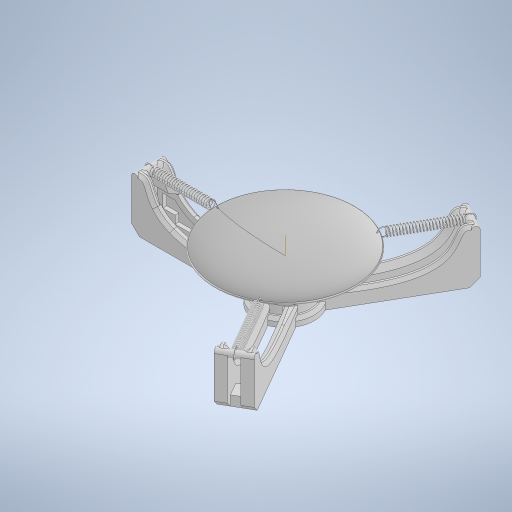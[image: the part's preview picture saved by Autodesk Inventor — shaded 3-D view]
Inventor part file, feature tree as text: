
AUTODESK INVENTOR PART (.ipt)
format: ipt  version: 2024.1 (Build 281209000, 209)  size: 2,633,216 bytes
history: native  units: mm
features: projected_geometry x39, sketch x23, extrude x18, fillet x5, chamfer x5, pattern_circular x4, other x3, mirror x2, revolve x1, helix x1, plane x1, imported_body x1
ambient origin geometry x8: Origin, YZ Plane, XZ Plane, XY Plane, X Axis, Y Axis, Z Axis, Center Point
bodies: Body1 (feature_tree), Body2 (feature_tree), Body3 (feature_tree), Body4 (feature_tree)
feature tree (103):
  other  "dish"
  revolve  "Revolution1"  [1 undecoded]
  extrude  "Extrusion2"  Depth=0.5mm
  pattern_circular  "Circular Pattern1"  Count=3 Angle=360.0deg
  extrude  "Extrusion3"  Depth=0.9mm
  fillet  "Fillet2"  Radius=73.4mm
  helix  "Coil1"  [1 undecoded]
  extrude  "Extrusion4"  Depth=1.2mm
  fillet  "Fillet3"  Radius=4.127824mm
  extrude  "Extrusion5"  Depth=65.0mm
  fillet  "Fillet4"  Radius=1.0mm
  fillet  "Fillet5"  Radius=0.45mm
  pattern_circular  "Circular Pattern2"  Count=3 Angle=360.0deg
  extrude  "Extrusion6"  Depth=10.0mm TaperAngle=0.0deg
  extrude  "Extrusion7"  Depth=15.0mm
  mirror  "Mirror1"
  pattern_circular  "Circular Pattern3"  Count=3 Angle=360.0deg
  extrude  "Extrusion10"  Depth=25.0mm
  pattern_circular  "Circular Pattern4"  Count=4  [1 undecoded]
  extrude  "Extrusion11"  Depth=12.5mm
  extrude  "Extrusion12"  Depth=2.5mm TaperAngle=0.0deg
  extrude  "Extrusion13"  Depth=2.5mm
  sketch  "Sketch16"  dims[d40=0.45mm]
  chamfer  "Chamfer1"  Distance=2.5mm
  extrude  "Extrusion14"  Depth=3.0mm
  chamfer  "Chamfer2"  Distance=8.0mm Angle=45.0deg
  fillet  "Fillet6"  Radius=4.75mm
  extrude  "Extrusion15"  Depth=3.0mm TaperAngle=45.0deg
  plane  "Work Plane1"
  mirror  "Mirror2"
  sketch  "Sketch20"  dims[d49=30.0mm d50=360.0deg d57=15.0mm]
  extrude  "Extrusion17"  Depth=3.0mm
  extrude  "Extrusion18"  Depth=3.0mm TaperAngle=0.0deg
  extrude  "Extrusion19"  TaperAngle=60.0deg  [1 undecoded]
  extrude  "Extrusion20"  Depth=3.0mm
  extrude  "Extrusion21"  Depth=3.0mm
  chamfer  "Chamfer3"  Distance=0.1mm
  extrude  "Extrusion22"  Depth=3.0mm
  chamfer  "Chamfer4"  Distance=0.1mm
  chamfer  "Chamfer5"  Distance=0.1mm
  sketch  "Sketch24"  dims[d71=10.9mm d72=2.5mm d73=0.0mm]
  sketch  "Sketch2"  dims[d4=70.5mm d5=1.9mm]
  sketch  "Sketch3"  dims[d6=8.0mm d7=0.5mm]
  sketch  "Sketch4"  dims[d8=0.95mm]
  projected_geometry  "Projected Loop1"
  other  "spring"
  sketch  "Sketch5"  dims[d9=90.0deg]
  sketch  "Sketch6"  dims[d10=1.5mm]
  sketch  "Sketch7"  dims[d11=69.0mm]
  sketch  "Sketch8"  dims[d12=0.0mm d13=0.0mm d14=30.0mm d15=360.0deg]
  sketch  "Sketch9"  dims[d17=9.65mm d18=0.9mm d19=73.4mm d20=1.0mm d21=0.0mm]
  imported_body  "base"
  sketch  "Sketch12"  dims[d22=0.45mm d23=1.2mm d24=4.127824mm]
  sketch  "Sketch13"  dims[d25=75.104637mm]
  sketch  "Sketch14"  dims[d26=2.3mm d27=60.0mm d28=240.0mm d29=0.0mm d30=90.0deg d31=90.0deg d32=0.0mm d33=0.0mm d34=65.0mm d35=1.0mm d36=0.0mm d37=0.45mm]
  projected_geometry  "Projected Loop2"
  projected_geometry  "Projected Loop3"
  sketch  "Sketch15"  dims[d38=0.0mm d39=0.0mm]
  sketch  "Sketch17"  dims[d41=3.0mm d42=30.0mm d43=360.0deg]
  sketch  "Sketch18"  dims[d45=10.0mm d46=0.0mm d47=10.0mm d48=0.0mm]
  projected_geometry  "Projected Loop4"
  sketch  "Sketch21"  dims[d58=10.0mm d59=0.0mm d60=30.0mm d61=360.0deg]
  projected_geometry  "Projected Loop6"
  sketch  "Sketch22"  dims[d63=25.0mm d66=25.0mm d67=40.0mm d68=0.0mm]
  projected_geometry  "Projected Loop7"
  projected_geometry  "Projected Loop8"
  projected_geometry  "Projected Loop9"
  other  "lock"
  sketch  "Sketch23"  dims[d69=12.5mm d70=12.5mm]
  projected_geometry  "Projected Loop10"
  projected_geometry  "Projected Loop11"
  projected_geometry  "Projected Loop12"
  projected_geometry  "Projected Loop13"
  projected_geometry  "Projected Loop14"
  projected_geometry  "Projected Loop15"
  projected_geometry  "Projected Loop16"
  projected_geometry  "Projected Loop17"
  projected_geometry  "Projected Loop18"
  projected_geometry  "Projected Loop19"
  projected_geometry  "Projected Loop20"
  projected_geometry  "Projected Loop21"
  projected_geometry  "Projected Loop22"
  projected_geometry  "Projected Loop23"
  projected_geometry  "Projected Loop24"
  projected_geometry  "Projected Loop25"
  projected_geometry  "Projected Loop26"
  projected_geometry  "Projected Loop27"
  sketch  "Sketch25"  dims[d74=25.0mm d75=2.5mm]
  sketch  "Sketch26"  dims[d77=50.0mm d78=2.5mm d79=0.0mm]
  projected_geometry  "Projected Loop28"
  projected_geometry  "Projected Loop29"
  projected_geometry  "Projected Loop30"
  projected_geometry  "Projected Loop31"
  projected_geometry  "Projected Loop32"
  projected_geometry  "Projected Loop33"
  projected_geometry  "Projected Loop34"
  projected_geometry  "Projected Loop35"
  projected_geometry  "Projected Loop36"
  sketch  "Sketch27"  dims[d81=2.5mm d82=8.0mm d83=8.0mm d84=2.0mm d85=45.0deg d86=4.75mm d87=0.0mm d88=5.0mm d89=2.0mm d90=45.0deg d91=5.0mm d92=4.0mm d93=0.0mm d95=60.0deg d115=8.0mm d116=0.1mm d118=0.1mm d119=0.1mm d120=0.1mm d121=0.1mm d122=0.1mm d123=0.0mm d124=0.0mm d125=50.0mm d126=0.1mm d127=0.1mm d128=0.1mm d129=10.0mm d130=0.0mm d131=8.0mm d132=0.0mm d133=60.0mm d134=3.0mm d135=0.0mm d136=15.0mm d137=0.0mm d138=2.0mm d139=2.0mm d140=45.0deg d141=0.2mm d142=0.2mm d143=0.2mm d144=0.2mm d145=0.2mm d146=0.5mm d147=0.0mm d148=3.0mm d149=2.0mm d150=45.0deg d151=3.0mm d152=2.0mm d153=45.0deg]
  projected_geometry  "Projected Loop37"
  projected_geometry  "Projected Loop38"
  projected_geometry  "Projected Loop39"
  projected_geometry  "Projected Loop40"
note: 4 required parameter values undecoded (feature->parameter linkage not recoverable at this tier; creation-order binding heuristic only, values carry confidence <= 0.55)